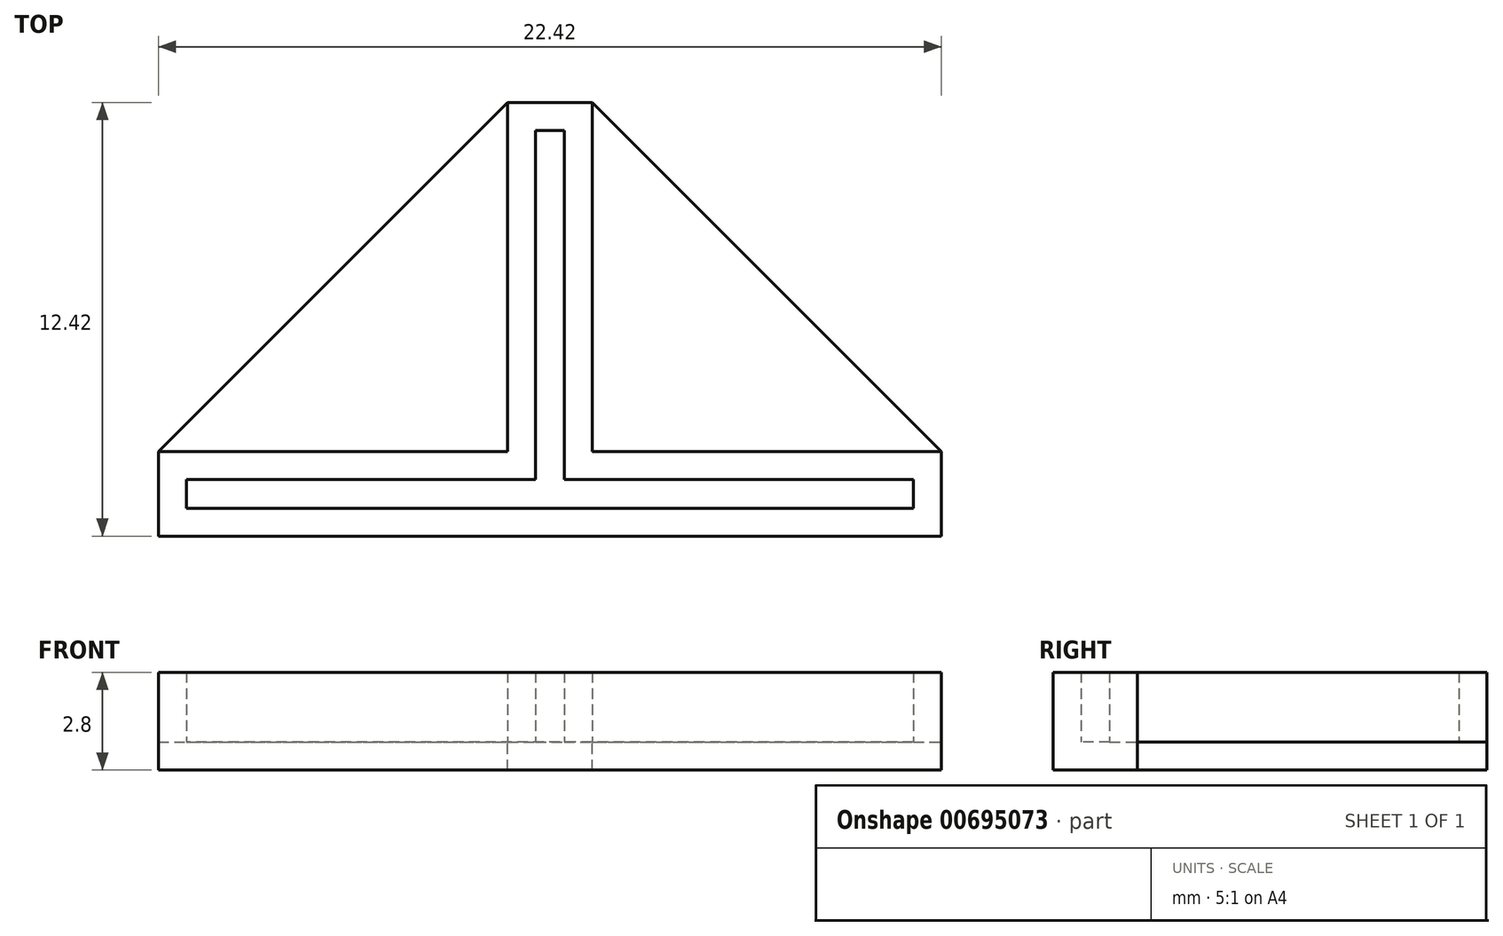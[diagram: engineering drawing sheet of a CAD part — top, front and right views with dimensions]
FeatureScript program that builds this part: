
annotation { "Feature Type Name" : "Feature", "Feature Type Description" : "" }
export const myFeature = defineFeature(function(context is Context, id is Id, definition is map)
    precondition{}
    {
        {
            var Q0;
            Q0=qCreatedBy(makeId("Top.planeOp"),FACE);
            var sketch = newSketch(context, id + "F0", { "sketchPlane" : qUnion([Q0])});
            skLineSegment(sketch, "E0", {"start": v(-0.4, 0.4) * mm, "end": v(-0.4, 10.4) * mm});
            skLineSegment(sketch, "E1", {"start": v(-0.4, 10.4) * mm, "end": v(0.4, 10.4) * mm});
            skLineSegment(sketch, "E2", {"start": v(0.4, 10.4) * mm, "end": v(0.41, 0.41) * mm});
            skLineSegment(sketch, "E3", {"start": v(0.4, 0.4) * mm, "end": v(10.4, 0.41) * mm});
            skLineSegment(sketch, "E4", {"start": v(10.4, 0.4) * mm, "end": v(10.4, -0.4) * mm});
            skLineSegment(sketch, "E5", {"start": v(10.4, -0.4) * mm, "end": v(0.4, -0.41) * mm});
            skLineSegment(sketch, "E6", {"start": v(0.41, -0.4) * mm, "end": v(0.41, -10.4) * mm});
            skLineSegment(sketch, "E7", {"start": v(0.4, -10.4) * mm, "end": v(-0.4, -10.4) * mm});
            skLineSegment(sketch, "E8", {"start": v(-0.4, -10.4) * mm, "end": v(-0.4, -0.4) * mm});
            skLineSegment(sketch, "E9", {"start": v(-0.4, -0.4) * mm, "end": v(-10.4, -0.4) * mm});
            skLineSegment(sketch, "E10", {"start": v(-10.4, -0.4) * mm, "end": v(-10.4, 0.4) * mm});
            skLineSegment(sketch, "E11", {"start": v(-10.4, 0.4) * mm, "end": v(-0.4, 0.4) * mm});
            skPoint(sketch, "E12", {"position": v(0, 10.4) * mm});
            skPoint(sketch, "E13", {"position": v(-10.4, 0) * mm});
            skLineSegment(sketch, "E14.0", {"start": v(-11.21, -1.21) * mm, "end": v(-11.21, 1.21) * mm});
            skLineSegment(sketch, "E14.1", {"start": v(1.21, 1.2) * mm, "end": v(11.21, 1.21) * mm});
            skLineSegment(sketch, "E14.2", {"start": v(1.2, 11.2) * mm, "end": v(1.21, 1.21) * mm});
            skLineSegment(sketch, "E14.3", {"start": v(-1.21, 11.2) * mm, "end": v(1.21, 11.2) * mm});
            skLineSegment(sketch, "E14.4", {"start": v(-1.21, 1.21) * mm, "end": v(-1.21, 11.2) * mm});
            skLineSegment(sketch, "E14.5", {"start": v(11.21, 1.21) * mm, "end": v(11.21, -1.21) * mm});
            skLineSegment(sketch, "E14.6", {"start": v(-11.21, 1.21) * mm, "end": v(-1.21, 1.21) * mm});
            skLineSegment(sketch, "E14.7", {"start": v(11.21, -1.2) * mm, "end": v(1.21, -1.21) * mm});
            skLineSegment(sketch, "E14.8", {"start": v(1.21, -1.21) * mm, "end": v(1.21, -11.2) * mm});
            skLineSegment(sketch, "E14.9", {"start": v(1.21, -11.2) * mm, "end": v(-1.21, -11.2) * mm});
            skLineSegment(sketch, "E14.10", {"start": v(-1.21, -11.2) * mm, "end": v(-1.21, -1.21) * mm});
            skLineSegment(sketch, "E14.11", {"start": v(-1.21, -1.21) * mm, "end": v(-11.21, -1.21) * mm});
            skLineSegment(sketch, "E15", {"start": v(-11.21, 1.2) * mm, "end": v(-1.2, 11.2) * mm});
            skLineSegment(sketch, "E16", {"start": v(1.2, 11.2) * mm, "end": v(11.21, 1.2) * mm});
            skLineSegment(sketch, "E17", {"start": v(11.21, -1.2) * mm, "end": v(1.2, -11.2) * mm});
            skLineSegment(sketch, "E18", {"start": v(-1.2, -11.2) * mm, "end": v(-11.21, -1.21) * mm});
            skLineSegment(sketch, "E19", {"start": v(-1.21, -1.21) * mm, "end": v(1.21, -1.21) * mm});
            skLineSegment(sketch, "E20", {"start": v(-0.4, -0.4) * mm, "end": v(0.4, -0.41) * mm});
            skSolve(sketch);
        }
        {
            var Q0;
            Q0=makeQuery(id+"F0.imprint","IMPRINT",FACE,{"disambiguationData":[TD([[makeQuery(id+"F0.imprint","IMPRINT",EDGE,{"derivedFrom":sQuery(id+"F0.wireOp",EDGE,"E0")}),1.0]])]});
            var Q1;
            {var subQ0=sQuery(id+"F0.wireOp",EDGE,"E20");Q1=makeQuery(id+"F0.imprint","IMPRINT",FACE,{"disambiguationData":[TD([[makeQuery(id+"F0.imprint","IMPRINT",EDGE,{"derivedFrom":subQ0}),-1.0]])]});}
            extrude(context, id + "F1", {"entities" : qUnion([Q0, Q1]), "depth" : 2 * mm, "offsetDistance" : 25 * mm});
        }
        {
            var Q0;
            Q0=makeQuery(id+"F0.imprint","IMPRINT",FACE,{"disambiguationData":[TD([[makeQuery(id+"F0.imprint","IMPRINT",EDGE,{"derivedFrom":sQuery(id+"F0.wireOp",EDGE,"E14.4")}),1.0]])]});
            var Q1;
            Q1=makeQuery(id+"F0.imprint","IMPRINT",FACE,{"disambiguationData":[TD([[makeQuery(id+"F0.imprint","IMPRINT",EDGE,{"derivedFrom":sQuery(id+"F0.wireOp",EDGE,"E14.1")}),1.0]])]});
            var Q2;
            Q2=makeQuery(id+"F0.imprint","IMPRINT",FACE,{"disambiguationData":[TD([[makeQuery(id+"F0.imprint","IMPRINT",EDGE,{"derivedFrom":sQuery(id+"F0.wireOp",EDGE,"E0")}),1.0]])]});
            var Q3;
            Q3=makeQuery(id+"F1.opExtrude","CAP_FACE",FACE,{"disambiguationData":[OSD([sQuery(id+"F0.wireOp",EDGE,"E0"),sQuery(id+"F0.wireOp",EDGE,"E1"),sQuery(id+"F0.wireOp",EDGE,"E2"),sQuery(id+"F0.wireOp",EDGE,"E3"),sQuery(id+"F0.wireOp",EDGE,"E4"),sQuery(id+"F0.wireOp",EDGE,"E5"),sQuery(id+"F0.wireOp",EDGE,"E6"),sQuery(id+"F0.wireOp",EDGE,"E7"),sQuery(id+"F0.wireOp",EDGE,"E8"),sQuery(id+"F0.wireOp",EDGE,"E9"),sQuery(id+"F0.wireOp",EDGE,"E10"),sQuery(id+"F0.wireOp",EDGE,"E11")])],"isStart":false});
            var Q4;
            Q4=makeQuery(id+"F0.imprint","IMPRINT",FACE,{"disambiguationData":[TD([[makeQuery(id+"F0.imprint","IMPRINT",EDGE,{"derivedFrom":sQuery(id+"F0.wireOp",EDGE,"E0")}),-1.0]])]});
            var Q5;
            {var subQ0=sQuery(id+"F0.wireOp",EDGE,"E20");Q5=makeQuery(id+"F0.imprint","IMPRINT",FACE,{"disambiguationData":[TD([[makeQuery(id+"F0.imprint","IMPRINT",EDGE,{"derivedFrom":subQ0}),-1.0]])]});}
            extrude(context, id + "F2", {"entities" : qUnion([Q0, Q1, Q2, Q3, Q4, Q5]), "operationType" : NewBodyOperationType.ADD, "oppositeDirection" : true, "depth" : 0.8 * mm, "offsetDistance" : 25 * mm});
        }
    });
